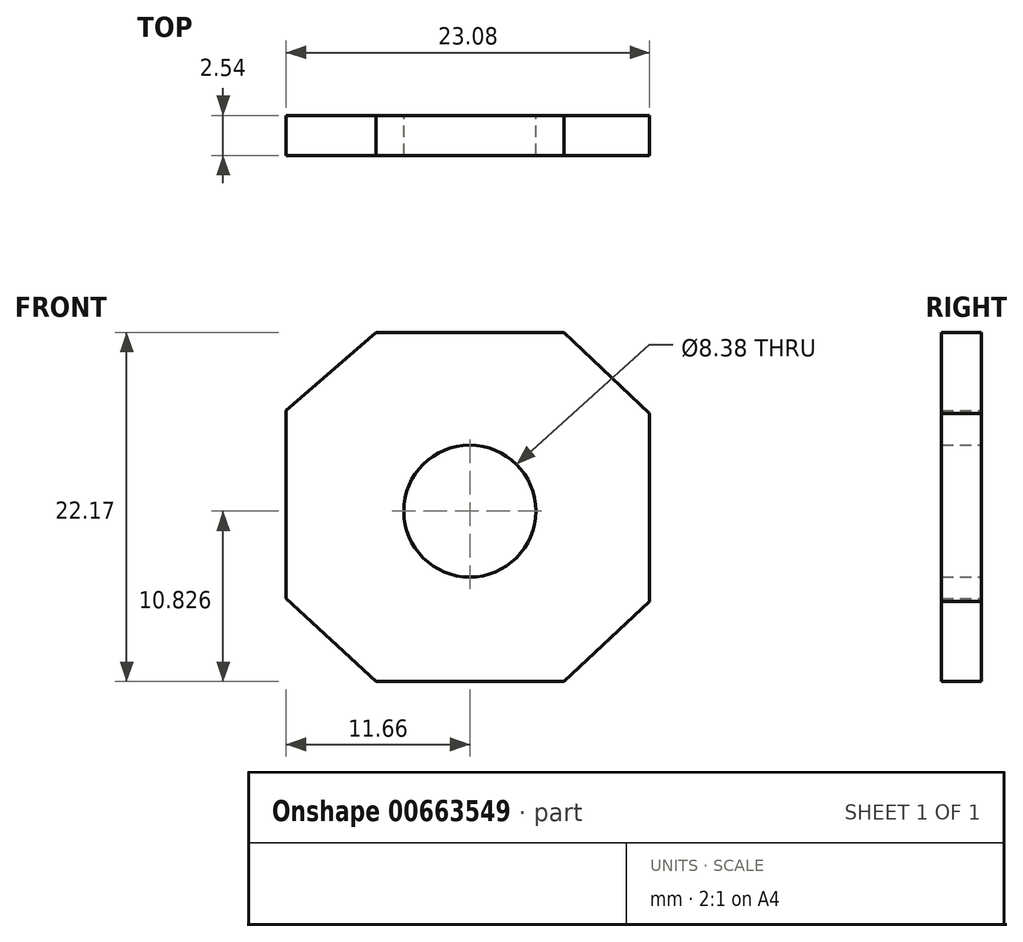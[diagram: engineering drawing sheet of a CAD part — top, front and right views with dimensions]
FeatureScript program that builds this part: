
annotation { "Feature Type Name" : "Feature", "Feature Type Description" : "" }
export const myFeature = defineFeature(function(context is Context, id is Id, definition is map)
    precondition{}
    {
        {
            var Q0;
            Q0=qCreatedBy(makeId("Front.planeOp"),FACE);
            var sketch = newSketch(context, id + "F0", { "sketchPlane" : qUnion([Q0])});
            skLineSegment(sketch, "E0", {"start": v(-11.66, 11.24) * mm, "end": v(-11.66, 17.21) * mm});
            skLineSegment(sketch, "E1", {"start": v(-11.66, 11.24) * mm, "end": v(-11.66, 5.28) * mm});
            skLineSegment(sketch, "E2", {"start": v(11.42, 11.07) * mm, "end": v(11.42, 5.1) * mm});
            skLineSegment(sketch, "E3", {"start": v(11.42, 11.07) * mm, "end": v(11.42, 17.04) * mm});
            skLineSegment(sketch, "E4", {"start": v(0, 0) * mm, "end": v(5.97, 0) * mm});
            skLineSegment(sketch, "E5", {"start": v(0, 0) * mm, "end": v(-5.97, 0) * mm});
            skLineSegment(sketch, "E6", {"start": v(0, 22.17) * mm, "end": v(5.97, 22.17) * mm});
            skLineSegment(sketch, "E7", {"start": v(0, 22.17) * mm, "end": v(-5.97, 22.17) * mm});
            skLineSegment(sketch, "E8", {"start": v(5.97, 0) * mm, "end": v(11.42, 5.1) * mm});
            skLineSegment(sketch, "E9", {"start": v(11.42, 17.04) * mm, "end": v(5.97, 22.17) * mm});
            skLineSegment(sketch, "E10", {"start": v(-5.97, 22.17) * mm, "end": v(-11.66, 17.21) * mm});
            skLineSegment(sketch, "E11", {"start": v(-11.66, 5.28) * mm, "end": v(-5.97, 0) * mm});
            skCircle(sketch, "E12", {"center": v(0, 10.83) * mm, "radius": 4.2 * mm});
            skSolve(sketch);
        }
        {
            var Q0;
            Q0 = qSketchRegion(id + "F0", true);
            extrude(context, id + "F1", {"entities" : qUnion([Q0]), "depth" : 2.54 * mm, "offsetDistance" : 25.4 * mm});
        }
    });
